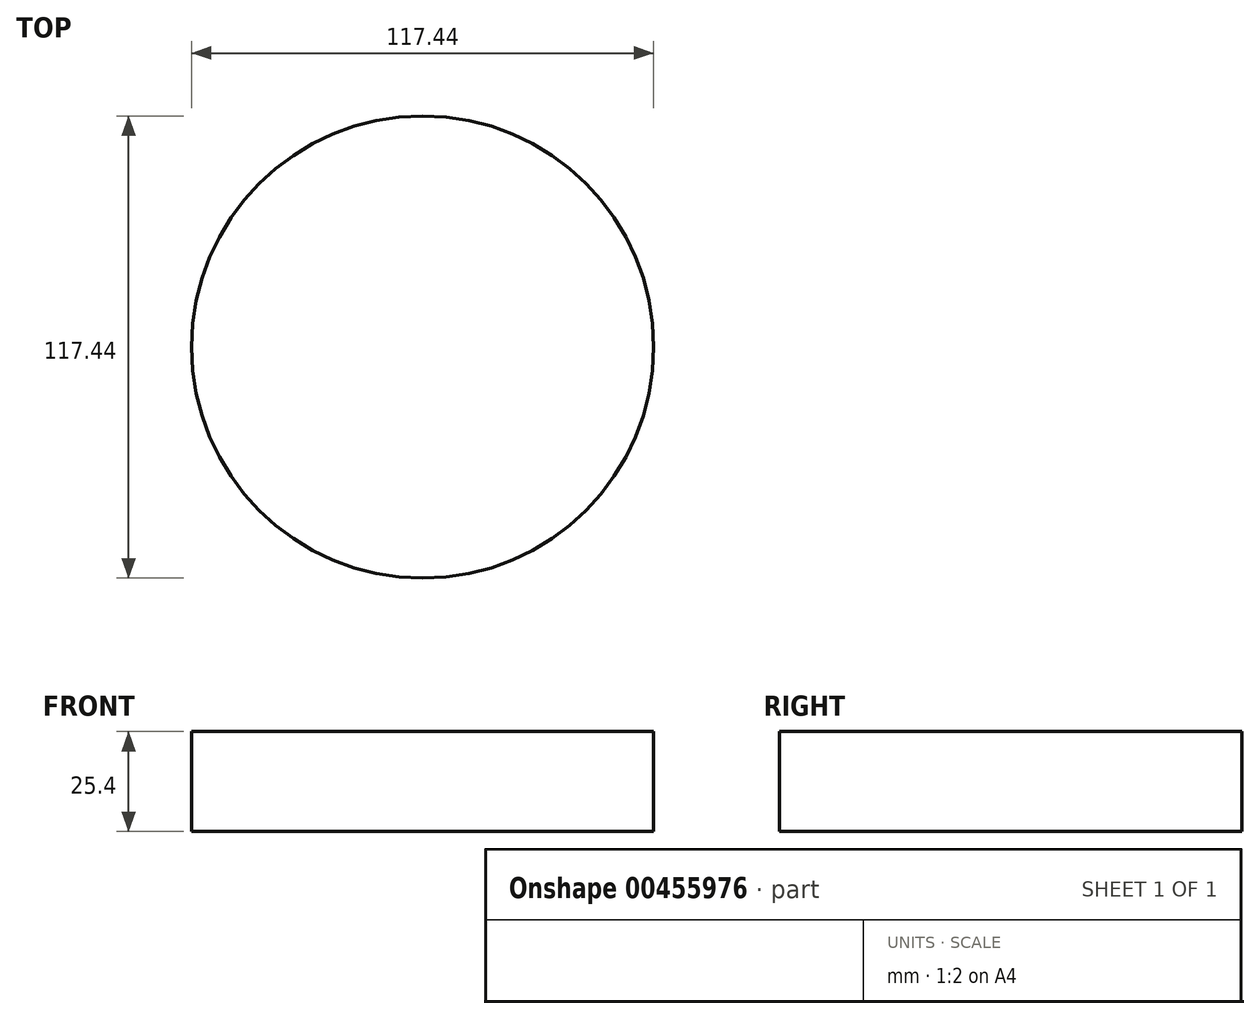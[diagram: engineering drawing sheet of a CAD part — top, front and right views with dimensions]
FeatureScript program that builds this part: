
annotation { "Feature Type Name" : "Feature", "Feature Type Description" : "" }
export const myFeature = defineFeature(function(context is Context, id is Id, definition is map)
    precondition{}
    {
        {
            var Q0;
            Q0=qCreatedBy(makeId("Top.planeOp"),FACE);
            var sketch = newSketch(context, id + "F0", { "sketchPlane" : qUnion([Q0])});
            skCircle(sketch, "E0", {"center": v(0, 0) * mm, "radius": 58.72 * mm});
            skSolve(sketch);
        }
        {
            var Q0;
            Q0=makeQuery(id+"F0.imprint","IMPRINT",FACE,{"disambiguationData":[TD([[makeQuery(id+"F0.imprint","IMPRINT",EDGE,{"derivedFrom":sQuery(id+"F0.wireOp",EDGE,"E0")}),1.0]])]});
            var Q1;
            Q1 = qSketchRegion(id + "F0", true);
            extrude(context, id + "F1", {"entities" : qUnion([Q0, Q1]), "depth" : 25.4 * mm});
        }
    });
